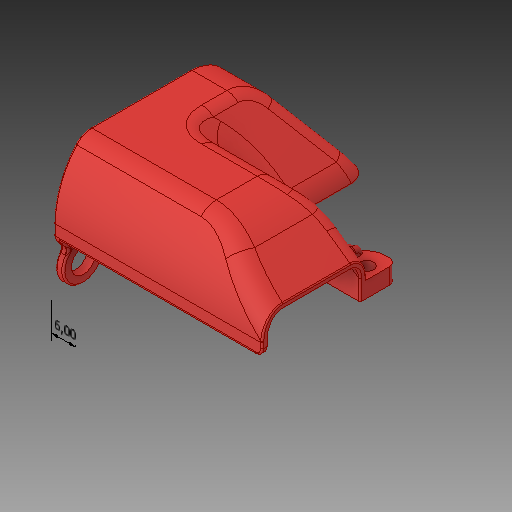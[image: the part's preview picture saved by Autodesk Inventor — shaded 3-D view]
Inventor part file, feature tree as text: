
AUTODESK INVENTOR PART (.ipt)
format: ipt  version: 2019.4 (Build 234330000, 330)  size: 2,835,968 bytes
history: native  units: in
note: dims shown in document units (in); Inventor stores cm internally (conversion verified against a paired STEP export)
features: other x7, fillet x7, extrude x4, sketch x4, plane x2, loft x2, projected_geometry x2
ambient origin geometry x8: Origin, YZ Plane, XZ Plane, XY Plane, X Axis, Y Axis, Z Axis, Center Point
bodies: Solid1 (feature_tree)
feature tree (28):
  other  "Annotations"
  plane  "Work Plane1"
  extrude  "Extrusion1"  Depth=0.315in TaperAngle=0.0deg
  plane  "Work Plane2"
  extrude  "Extrusion2"  Depth=0.0197in
  fillet  "Fillet1"  Radius=0.2362in
  extrude  "Extrusion3"  Depth=0.3937in
  fillet  "Fillet2"  Radius=0.3937in
  fillet  "Fillet3"  Radius=0.8661in
  fillet  "Fillet4"  Radius=0.3937in
  fillet  "Fillet5"  Radius=0.3937in
  fillet  "Fillet6"  Radius=0.2362in
  extrude  "Extrusion4"  Depth=0.1969in
  loft  "Loft1"
  loft  "Loft3"
  fillet  "Fillet8"  Radius=0.0157in
  sketch  "Sketch3"  dims[d4=-0.0394in d5=0.315in d6=0.0in]
  sketch  "Sketch4"  dims[d7=0.2756in d8=0.0in d15=0.0197in d16=0.2362in]
  sketch  "Sketch5"  dims[d17=0.2362in d18=0.3937in d19=0.3937in d20=0.8661in d22=0.3937in d23=0.3937in d24=0.2362in]
  other  "Edges1"
  other  "Edges3"
  sketch  "Sketch11"  dims[d25=0.2362in d26=0.1969in d27=0.1575in d28=0.3937in d29=0.0in d30=0.0157in d31=0.0157in d32=0.315in d33=0.315in d34=0.0591in d37=0.3937in d38=0.0in d39=0.0in d40=90.0deg d44=90.0deg d45=0.0in d46=90.0deg d58=0.0in d59=90.0deg d60=0.0in d61=90.0deg d62=0.0118in d10=0.1674in d11=0.0787in d12=-0.4302in d13=-0.17in d14=0.2362in d9=0.2838in]
  other  "Edges5"
  other  "[a]_connector_cover"
  projected_geometry  "Project Cut Edges1"
  projected_geometry  "Project Cut Edges2"
  other  "Linear Dimension 1"
  other  "Linear Dimension 2"
